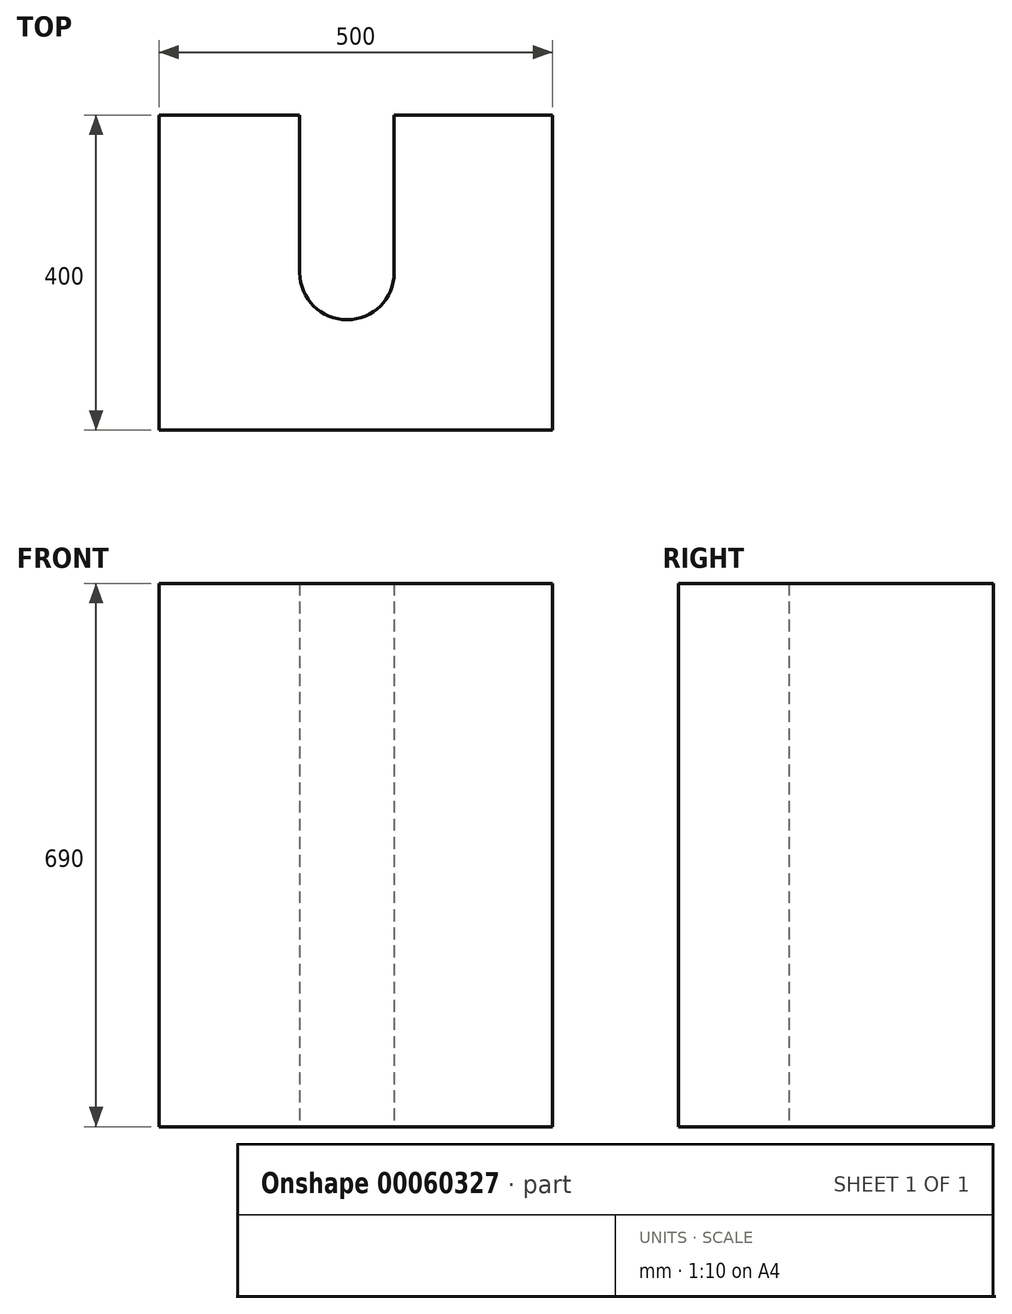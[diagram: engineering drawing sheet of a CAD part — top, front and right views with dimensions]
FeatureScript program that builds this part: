
annotation { "Feature Type Name" : "Feature", "Feature Type Description" : "" }
export const myFeature = defineFeature(function(context is Context, id is Id, definition is map)
    precondition{}
    {
        {
            var Q0;
            Q0=qCreatedBy(makeId("Top.planeOp"),FACE);
            var sketch = newSketch(context, id + "F0", { "sketchPlane" : qUnion([Q0])});
            skLineSegment(sketch, "E0.bottom", {"start": v(0, -400) * mm, "end": v(0, -400) * mm});
            skLineSegment(sketch, "E0.top", {"start": v(0, 0) * mm, "end": v(0, 0) * mm});
            skLineSegment(sketch, "E0.left", {"start": v(0, -400) * mm, "end": v(0, 0) * mm});
            skLineSegment(sketch, "E0.right", {"start": v(0, -400) * mm, "end": v(0, 0) * mm});
            skLineSegment(sketch, "E1.bottom", {"start": v(-500, 0) * mm, "end": v(0, 0) * mm});
            skLineSegment(sketch, "E1.top", {"start": v(-500, -400) * mm, "end": v(0, -400) * mm});
            skLineSegment(sketch, "E1.left", {"start": v(-500, 0) * mm, "end": v(-500, -400) * mm});
            skLineSegment(sketch, "E1.right", {"start": v(0, 0) * mm, "end": v(0, -400) * mm});
            skLineSegment(sketch, "E2", {"start": v(-321.12, 0) * mm, "end": v(-321.12, -200) * mm});
            skLineSegment(sketch, "E3", {"start": v(-201.12, 0) * mm, "end": v(-201.12, -200) * mm});
            skArc(sketch, "E4", {"start": v(-201.12, -200) * mm, "mid": v(-261.12, -260) * mm, "end": v(-321.12, -200) * mm});
            skSolve(sketch);
        }
        {
            var Q0;
            Q0=makeQuery(id+"F0.imprint","IMPRINT",FACE,{"disambiguationData":[TD([[makeQuery(id+"F0.imprint","IMPRINT",EDGE,{"derivedFrom":sQuery(id+"F0.wireOp",EDGE,"E1.top")}),1.0]])]});
            extrude(context, id + "F1", {"entities" : qUnion([Q0]), "depth" : 690 * mm});
        }
    });
